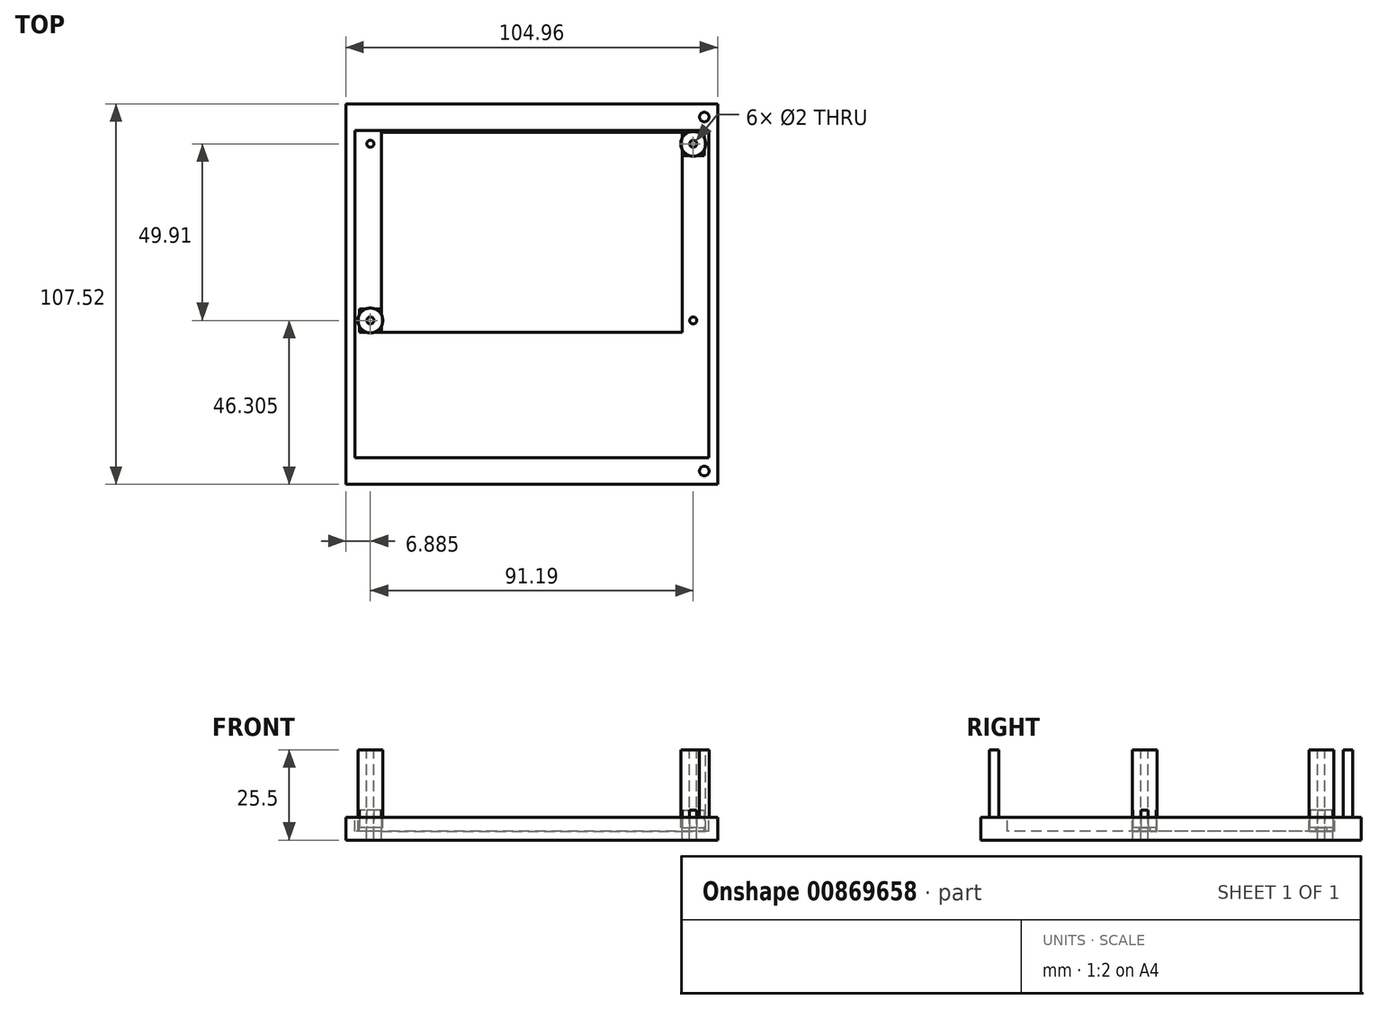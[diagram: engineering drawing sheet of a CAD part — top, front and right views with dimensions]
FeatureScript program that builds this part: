
annotation { "Feature Type Name" : "Feature", "Feature Type Description" : "" }
export const myFeature = defineFeature(function(context is Context, id is Id, definition is map)
    precondition{}
    {
        {
            var Q0;
            Q0=qCreatedBy(makeId("Top.planeOp"),FACE);
            var sketch = newSketch(context, id + "F0", { "sketchPlane" : qUnion([Q0])});
            skLineSegment(sketch, "E0.bottom", {"start": v(-42.48, 28.26) * mm, "end": v(42.48, 28.26) * mm});
            skLineSegment(sketch, "E0.top", {"start": v(-42.48, -28.26) * mm, "end": v(42.48, -28.26) * mm});
            skLineSegment(sketch, "E0.left", {"start": v(-42.48, 28.26) * mm, "end": v(-42.48, -28.26) * mm});
            skLineSegment(sketch, "E0.right", {"start": v(42.48, 28.26) * mm, "end": v(42.48, -28.26) * mm});
            skLineSegment(sketch, "E1.bottom", {"start": v(-42.48, 28.26) * mm, "end": v(-48.7, 28.26) * mm});
            skLineSegment(sketch, "E1.top", {"start": v(-42.48, 21.65) * mm, "end": v(-48.7, 21.65) * mm});
            skLineSegment(sketch, "E1.left", {"start": v(-42.48, 28.26) * mm, "end": v(-42.48, 21.65) * mm});
            skLineSegment(sketch, "E1.right", {"start": v(-48.7, 28.26) * mm, "end": v(-48.7, 21.65) * mm});
            skLineSegment(sketch, "E2.MirrorCS", {"start": v(42.48, 28.26) * mm, "end": v(48.7, 28.26) * mm});
            skLineSegment(sketch, "E3.MirrorCS", {"start": v(48.7, 28.26) * mm, "end": v(48.7, 21.65) * mm});
            skLineSegment(sketch, "E4.MirrorCS", {"start": v(42.48, 21.65) * mm, "end": v(48.7, 21.65) * mm});
            skLineSegment(sketch, "E5.MirrorCS", {"start": v(-42.48, -28.26) * mm, "end": v(-48.7, -28.26) * mm});
            skLineSegment(sketch, "E6.MirrorCS", {"start": v(42.48, -28.26) * mm, "end": v(48.7, -28.26) * mm});
            skLineSegment(sketch, "E7.MirrorCS", {"start": v(48.7, -28.26) * mm, "end": v(48.7, -21.65) * mm});
            skLineSegment(sketch, "E8.MirrorCS", {"start": v(42.48, -21.65) * mm, "end": v(48.7, -21.65) * mm});
            skLineSegment(sketch, "E9.MirrorCS", {"start": v(-42.48, -21.65) * mm, "end": v(-48.7, -21.65) * mm});
            skLineSegment(sketch, "E10.MirrorCS", {"start": v(-48.7, -28.26) * mm, "end": v(-48.7, -21.65) * mm});
            skCircle(sketch, "E11", {"center": v(-45.6, 24.96) * mm, "radius": 1 * mm});
            skPoint(sketch, "E11.centerSnap0", {"position": v(-45.6, 28.26) * mm});
            skPoint(sketch, "E11.centerSnap1", {"position": v(-42.48, 24.96) * mm});
            skCircle(sketch, "E12.MirrorC", {"center": v(45.6, 24.96) * mm, "radius": 1 * mm});
            skCircle(sketch, "E13.MirrorC", {"center": v(-45.6, -24.96) * mm, "radius": 1 * mm});
            skCircle(sketch, "E14.MirrorC", {"center": v(45.6, -24.96) * mm, "radius": 1 * mm});
            skLineSegment(sketch, "E15.bottom", {"start": v(52.48, 36.26) * mm, "end": v(-52.48, 36.26) * mm});
            skLineSegment(sketch, "E15.top", {"start": v(52.48, -71.26) * mm, "end": v(-52.48, -71.26) * mm});
            skLineSegment(sketch, "E15.left", {"start": v(52.48, 36.26) * mm, "end": v(52.48, -71.26) * mm});
            skLineSegment(sketch, "E15.right", {"start": v(-52.48, 36.26) * mm, "end": v(-52.48, -71.26) * mm});
            skSolve(sketch);
        }
        {
            var Q0;
            Q0=makeQuery(id+"F0.imprint","IMPRINT",FACE,{"disambiguationData":[TD([[makeQuery(id+"F0.imprint","IMPRINT",EDGE,{"derivedFrom":sQuery(id+"F0.wireOp",EDGE,"E0.bottom")}),1.0]])]});
            var Q1;
            {var subQ0=sQuery(id+"F0.wireOp",EDGE,"E5.MirrorCS");Q1=makeQuery(id+"F0.imprint","IMPRINT",FACE,{"disambiguationData":[TD([[makeQuery(id+"F0.imprint","IMPRINT",EDGE,{"derivedFrom":subQ0}),-1.0]])]});}
            var Q2;
            Q2=makeQuery(id+"F0.imprint","IMPRINT",FACE,{"disambiguationData":[TD([[makeQuery(id+"F0.imprint","IMPRINT",EDGE,{"derivedFrom":sQuery(id+"F0.wireOp",EDGE,"E1.bottom")}),1.0]])]});
            var Q3;
            Q3=makeQuery(id+"F0.imprint","IMPRINT",FACE,{"disambiguationData":[TD([[makeQuery(id+"F0.imprint","IMPRINT",EDGE,{"derivedFrom":sQuery(id+"F0.wireOp",EDGE,"E11")}),1.0]])]});
            var Q4;
            Q4=makeQuery(id+"F0.imprint","IMPRINT",FACE,{"disambiguationData":[TD([[makeQuery(id+"F0.imprint","IMPRINT",EDGE,{"derivedFrom":sQuery(id+"F0.wireOp",EDGE,"E13.MirrorC")}),-1.0]])]});
            var Q5;
            {var subQ1=sQuery(id+"F0.wireOp",EDGE,"E6.MirrorCS");Q5=makeQuery(id+"F0.imprint","IMPRINT",FACE,{"disambiguationData":[TD([[makeQuery(id+"F0.imprint","IMPRINT",EDGE,{"derivedFrom":subQ1}),1.0]])]});}
            var Q6;
            Q6=makeQuery(id+"F0.imprint","IMPRINT",FACE,{"disambiguationData":[TD([[makeQuery(id+"F0.imprint","IMPRINT",EDGE,{"derivedFrom":sQuery(id+"F0.wireOp",EDGE,"E14.MirrorC")}),1.0]])]});
            var Q7;
            {var subQ1=sQuery(id+"F0.wireOp",EDGE,"E2.MirrorCS");Q7=makeQuery(id+"F0.imprint","IMPRINT",FACE,{"disambiguationData":[TD([[makeQuery(id+"F0.imprint","IMPRINT",EDGE,{"derivedFrom":subQ1}),-1.0]])]});}
            var Q8;
            Q8=makeQuery(id+"F0.imprint","IMPRINT",FACE,{"disambiguationData":[TD([[makeQuery(id+"F0.imprint","IMPRINT",EDGE,{"derivedFrom":sQuery(id+"F0.wireOp",EDGE,"E12.MirrorC")}),-1.0]])]});
            var Q9;
            {var subQ4=sQuery(id+"F0.wireOp",EDGE,"E0.bottom");Q9=makeQuery(id+"F0.imprint","IMPRINT",FACE,{"disambiguationData":[TD([[makeQuery(id+"F0.imprint","IMPRINT",EDGE,{"derivedFrom":subQ4}),-1.0]])]});}
            extrude(context, id + "F1", {"entities" : qUnion([Q0, Q1, Q2, Q3, Q4, Q5, Q6, Q7, Q8, Q9]), "oppositeDirection" : true, "depth" : 3.5 * mm, "offsetDistance" : 25 * mm});
        }
        {
            var Q0;
            Q0=makeQuery(id+"F0.imprint","IMPRINT",FACE,{"disambiguationData":[TD([[makeQuery(id+"F0.imprint","IMPRINT",EDGE,{"derivedFrom":sQuery(id+"F0.wireOp",EDGE,"E0.bottom")}),1.0]])]});
            var Q1;
            {var subQ0=sQuery(id+"F0.wireOp",EDGE,"E5.MirrorCS");Q1=makeQuery(id+"F0.imprint","IMPRINT",FACE,{"disambiguationData":[TD([[makeQuery(id+"F0.imprint","IMPRINT",EDGE,{"derivedFrom":subQ0}),-1.0]])]});}
            var Q2;
            Q2=makeQuery(id+"F0.imprint","IMPRINT",FACE,{"disambiguationData":[TD([[makeQuery(id+"F0.imprint","IMPRINT",EDGE,{"derivedFrom":sQuery(id+"F0.wireOp",EDGE,"E1.bottom")}),1.0]])]});
            var Q3;
            {var subQ1=sQuery(id+"F0.wireOp",EDGE,"E2.MirrorCS");Q3=makeQuery(id+"F0.imprint","IMPRINT",FACE,{"disambiguationData":[TD([[makeQuery(id+"F0.imprint","IMPRINT",EDGE,{"derivedFrom":subQ1}),-1.0]])]});}
            var Q4;
            {var subQ1=sQuery(id+"F0.wireOp",EDGE,"E6.MirrorCS");Q4=makeQuery(id+"F0.imprint","IMPRINT",FACE,{"disambiguationData":[TD([[makeQuery(id+"F0.imprint","IMPRINT",EDGE,{"derivedFrom":subQ1}),1.0]])]});}
            var Q5;
            Q5=makeQuery(id+"F0.imprint","IMPRINT",FACE,{"disambiguationData":[TD([[makeQuery(id+"F0.imprint","IMPRINT",EDGE,{"derivedFrom":sQuery(id+"F0.wireOp",EDGE,"E13.MirrorC")}),-1.0]])]});
            var Q6;
            Q6=makeQuery(id+"F0.imprint","IMPRINT",FACE,{"disambiguationData":[TD([[makeQuery(id+"F0.imprint","IMPRINT",EDGE,{"derivedFrom":sQuery(id+"F0.wireOp",EDGE,"E11")}),1.0]])]});
            var Q7;
            Q7=makeQuery(id+"F0.imprint","IMPRINT",FACE,{"disambiguationData":[TD([[makeQuery(id+"F0.imprint","IMPRINT",EDGE,{"derivedFrom":sQuery(id+"F0.wireOp",EDGE,"E12.MirrorC")}),-1.0]])]});
            var Q8;
            Q8=makeQuery(id+"F0.imprint","IMPRINT",FACE,{"disambiguationData":[TD([[makeQuery(id+"F0.imprint","IMPRINT",EDGE,{"derivedFrom":sQuery(id+"F0.wireOp",EDGE,"E14.MirrorC")}),1.0]])]});
            var Q9;
            {var subQ4=sQuery(id+"F0.wireOp",EDGE,"E0.bottom");Q9=makeQuery(id+"F0.imprint","IMPRINT",FACE,{"disambiguationData":[TD([[makeQuery(id+"F0.imprint","IMPRINT",EDGE,{"derivedFrom":subQ4}),-1.0]])]});}
            extrude(context, id + "F2", {"entities" : qUnion([Q0, Q1, Q2, Q3, Q4, Q5, Q6, Q7, Q8, Q9]), "operationType" : NewBodyOperationType.ADD, "depth" : 22 * mm, "offsetDistance" : 25 * mm});
        }
        {
            var Q0;
            Q0=makeQuery(id+"F2.opExtrude","CAP_FACE",FACE,{"disambiguationData":[OSD([sQuery(id+"F0.wireOp",EDGE,"E0.bottom"),sQuery(id+"F0.wireOp",EDGE,"E0.top"),sQuery(id+"F0.wireOp",EDGE,"E0.left"),sQuery(id+"F0.wireOp",EDGE,"E0.right"),sQuery(id+"F0.wireOp",EDGE,"E1.left"),sQuery(id+"F0.wireOp",EDGE,"E15.bottom"),sQuery(id+"F0.wireOp",EDGE,"E15.top"),sQuery(id+"F0.wireOp",EDGE,"E15.left"),sQuery(id+"F0.wireOp",EDGE,"E15.right")])],"isStart":false});
            shell(context, id + "F3", {"entities" : qUnion([Q0]), "thickness" : 2.5 * mm});
        }
        {
            var Q0;
            {var subQ4=sQuery(id+"F0.wireOp",EDGE,"E0.bottom");Q0=makeQuery(id+"F0.imprint","IMPRINT",FACE,{"disambiguationData":[TD([[makeQuery(id+"F0.imprint","IMPRINT",EDGE,{"derivedFrom":subQ4}),-1.0]])]});}
            extrude(context, id + "F4", {"entities" : qUnion([Q0]), "operationType" : NewBodyOperationType.REMOVE, "endBound" : BoundingType.THROUGH_ALL, "oppositeDirection" : true, "depth" : 25 * mm, "offsetDistance" : 25 * mm});
        }
        {
            var Q0;
            Q0=makeQuery(id+"F0.imprint","IMPRINT",FACE,{"disambiguationData":[TD([[makeQuery(id+"F0.imprint","IMPRINT",EDGE,{"derivedFrom":sQuery(id+"F0.wireOp",EDGE,"E13.MirrorC")}),-1.0]])]});
            var Q1;
            Q1=makeQuery(id+"F0.imprint","IMPRINT",FACE,{"disambiguationData":[TD([[makeQuery(id+"F0.imprint","IMPRINT",EDGE,{"derivedFrom":sQuery(id+"F0.wireOp",EDGE,"E12.MirrorC")}),-1.0]])]});
            var Q2;
            Q2=makeQuery(id+"F0.imprint","IMPRINT",FACE,{"disambiguationData":[TD([[makeQuery(id+"F0.imprint","IMPRINT",EDGE,{"derivedFrom":sQuery(id+"F0.wireOp",EDGE,"E14.MirrorC")}),1.0]])]});
            var Q3;
            Q3=makeQuery(id+"F0.imprint","IMPRINT",FACE,{"disambiguationData":[TD([[makeQuery(id+"F0.imprint","IMPRINT",EDGE,{"derivedFrom":sQuery(id+"F0.wireOp",EDGE,"E11")}),1.0]])]});
            extrude(context, id + "F5", {"entities" : qUnion([Q0, Q1, Q2, Q3]), "depth" : 5 * mm, "offsetDistance" : 25 * mm});
        }
        {
            var Q0;
            Q0=makeQuery(id+"F5.opExtrude","CAP_FACE",FACE,{"disambiguationData":[OSD([sQuery(id+"F0.wireOp",EDGE,"E11")])],"isStart":true});
            var Q1;
            Q1=makeQuery(id+"F5.opExtrude","CAP_FACE",FACE,{"disambiguationData":[OSD([sQuery(id+"F0.wireOp",EDGE,"E13.MirrorC")])],"isStart":true});
            var Q2;
            Q2=makeQuery(id+"F5.opExtrude","CAP_FACE",FACE,{"disambiguationData":[OSD([sQuery(id+"F0.wireOp",EDGE,"E14.MirrorC")])],"isStart":true});
            var Q3;
            Q3=makeQuery(id+"F5.opExtrude","CAP_FACE",FACE,{"disambiguationData":[OSD([sQuery(id+"F0.wireOp",EDGE,"E12.MirrorC")])],"isStart":true});
            extrude(context, id + "F6", {"entities" : qUnion([Q0, Q1, Q2, Q3]), "depth" : 1 * mm, "offsetDistance" : 25 * mm});
        }
        {
            var Q0;
            Q0=makeQuery(id+"F3.opShell","OFFSET_FACE",FACE,{"disambiguationData":[OSD([sQuery(id+"F0.wireOp",EDGE,"E15.bottom")])]});
            extrude(context, id + "F7", {"entities" : qUnion([Q0]), "operationType" : NewBodyOperationType.ADD, "depth" : 5 * mm, "offsetDistance" : 25 * mm});
        }
        {
            var Q0;
            Q0=makeQuery(id+"F3.opShell","OFFSET_FACE",FACE,{"disambiguationData":[OSD([sQuery(id+"F0.wireOp",EDGE,"E15.top")])]});
            extrude(context, id + "F8", {"entities" : qUnion([Q0]), "operationType" : NewBodyOperationType.ADD, "depth" : 5 * mm, "offsetDistance" : 25 * mm});
        }
        {
            var Q0;
            {var subQ0=sQuery(id+"F0.wireOp",EDGE,"E15.bottom");Q0=makeQuery(id+"F7.boolean.opBoolean","MERGE",FACE,{"derivedFrom":[makeQuery(id+"F2.opExtrude","CAP_FACE",FACE,{"disambiguationData":[OSD([subQ0,sQuery(id+"F0.wireOp",EDGE,"E15.top"),sQuery(id+"F0.wireOp",EDGE,"E15.left"),sQuery(id+"F0.wireOp",EDGE,"E15.right")])],"isStart":false}),makeQuery(id+"F7.opExtrude","SWEPT_FACE",FACE,{"disambiguationData":[OSD([subQ0]),TDD([makeQuery(id+"F3.opShell","OFFSET_EDGE",EDGE,{"disambiguationData":[OSD([subQ0]),TDD([makeQuery(id+"F2.opExtrude","CAP_EDGE",EDGE,{"disambiguationData":[OSD([subQ0])],"isStart":false})])]})])]})]});}
            var sketch = newSketch(context, id + "F9", { "sketchPlane" : qUnion([Q0])});
            skCircle(sketch, "E16", {"center": v(-48.73, 32.5) * mm, "radius": 1.35 * mm});
            skCircle(sketch, "E17.MirrorC", {"center": v(48.73, 32.5) * mm, "radius": 1.35 * mm});
            skCircle(sketch, "E18", {"center": v(-48.73, -67.51) * mm, "radius": 1.35 * mm});
            skCircle(sketch, "E19.MirrorC", {"center": v(48.73, -67.51) * mm, "radius": 1.35 * mm});
            skSolve(sketch);
        }
        {
            var Q0;
            Q0=makeQuery(id+"F9.imprint","IMPRINT",FACE,{"disambiguationData":[TD([[makeQuery(id+"F9.imprint","IMPRINT",EDGE,{"derivedFrom":sQuery(id+"F9.wireOp",EDGE,"E16")}),1.0]])]});
            var Q1;
            Q1=makeQuery(id+"F9.imprint","IMPRINT",FACE,{"disambiguationData":[TD([[makeQuery(id+"F9.imprint","IMPRINT",EDGE,{"derivedFrom":sQuery(id+"F9.wireOp",EDGE,"E17.MirrorC")}),-1.0]])]});
            var Q2;
            Q2=makeQuery(id+"F9.imprint","IMPRINT",FACE,{"disambiguationData":[TD([[makeQuery(id+"F9.imprint","IMPRINT",EDGE,{"derivedFrom":sQuery(id+"F9.wireOp",EDGE,"E18")}),1.0]])]});
            var Q3;
            Q3=makeQuery(id+"F9.imprint","IMPRINT",FACE,{"disambiguationData":[TD([[makeQuery(id+"F9.imprint","IMPRINT",EDGE,{"derivedFrom":sQuery(id+"F9.wireOp",EDGE,"E19.MirrorC")}),-1.0]])]});
            extrude(context, id + "F10", {"entities" : qUnion([Q0, Q1, Q2, Q3]), "operationType" : NewBodyOperationType.REMOVE, "oppositeDirection" : true, "depth" : 19.05 * mm, "offsetDistance" : 25 * mm});
        }
    });
